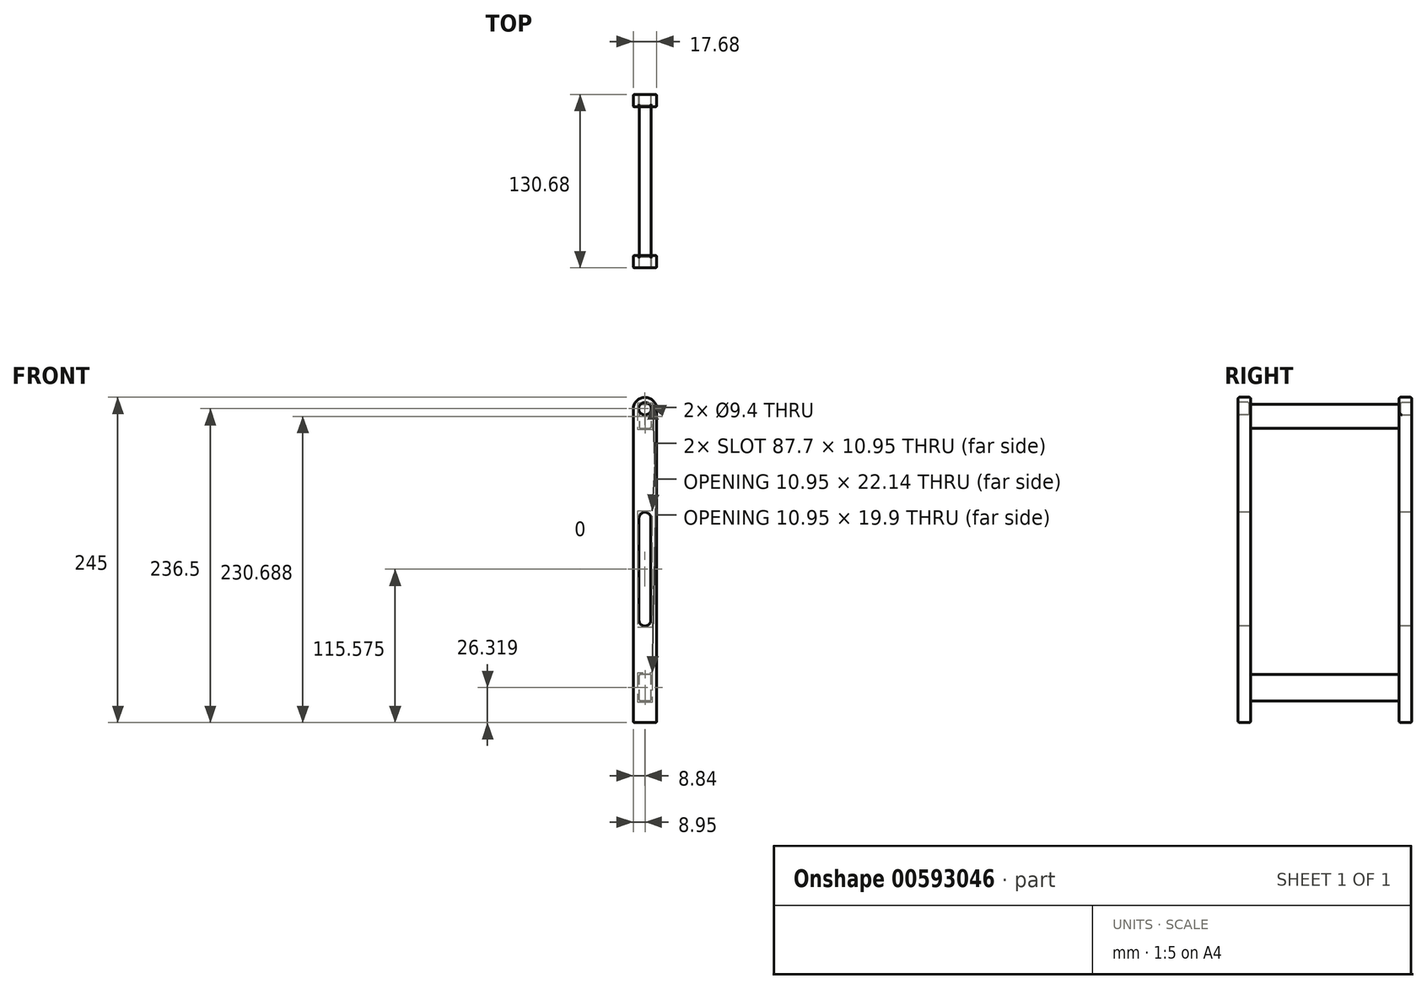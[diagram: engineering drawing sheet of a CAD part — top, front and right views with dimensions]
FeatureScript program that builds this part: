
annotation { "Feature Type Name" : "Feature", "Feature Type Description" : "" }
export const myFeature = defineFeature(function(context is Context, id is Id, definition is map)
    precondition{}
    {
        {
            var Q0;
            Q0=qCreatedBy(makeId("Front.planeOp"),FACE);
            var sketch = newSketch(context, id + "F0", { "sketchPlane" : qUnion([Q0])});
            skLineSegment(sketch, "E0.top", {"start": v(-8.84, -118.08) * mm, "end": v(8.84, -118.08) * mm});
            skLineSegment(sketch, "E0.left", {"start": v(-8.84, 118.08) * mm, "end": v(-8.84, -118.08) * mm});
            skLineSegment(sketch, "E0.right", {"start": v(8.84, 118.08) * mm, "end": v(8.84, -118.08) * mm});
            skPoint(sketch, "E0.middle", {"position": v(0, 0) * mm});
            skArc(sketch, "E1", {"start": v(-8.84, 118.08) * mm, "mid": v(0, 126.92) * mm, "end": v(8.84, 118.08) * mm});
            skSolve(sketch);
        }
        {
            var Q0;
            Q0=qSketchRegion(id+"F0",true);
            extrude(context, id + "F1", {"entities" : qUnion([Q0]), "depth" : 9.4 * mm});
        }
        {
            var Q0;
            Q0=makeQuery(id+"F1.opExtrude","CAP_FACE",FACE,{"disambiguationData":[OSD([sQuery(id+"F0.wireOp",EDGE,"E0.top"),sQuery(id+"F0.wireOp",EDGE,"E0.left"),sQuery(id+"F0.wireOp",EDGE,"E0.right"),sQuery(id+"F0.wireOp",EDGE,"E1")])],"isStart":false});
            var sketch = newSketch(context, id + "F2", { "sketchPlane" : qUnion([Q0])});
            skLineSegment(sketch, "E2.bottom", {"start": v(4.58, -101.83) * mm, "end": v(-4.37, -101.83) * mm});
            skLineSegment(sketch, "E2.top", {"start": v(4.58, -81.7) * mm, "end": v(-4.37, -81.7) * mm});
            skLineSegment(sketch, "E2.left", {"start": v(4.58, -101.83) * mm, "end": v(4.58, -81.7) * mm});
            skLineSegment(sketch, "E2.right", {"start": v(-4.37, -101.83) * mm, "end": v(-4.37, -81.7) * mm});
            skLineSegment(sketch, "E3.bottom", {"start": v(-4.36, 121.56) * mm, "end": v(4.59, 121.56) * mm});
            skLineSegment(sketch, "E3.top", {"start": v(-4.36, 103.66) * mm, "end": v(4.59, 103.66) * mm});
            skLineSegment(sketch, "E3.left", {"start": v(-4.36, 121.56) * mm, "end": v(-4.36, 103.66) * mm});
            skLineSegment(sketch, "E3.right", {"start": v(4.59, 121.56) * mm, "end": v(4.59, 103.66) * mm});
            skSolve(sketch);
        }
        {
            var Q0;
            Q0=makeQuery(id+"F2.imprint","IMPRINT",FACE,{"disambiguationData":[TD([[makeQuery(id+"F2.imprint","IMPRINT",EDGE,{"derivedFrom":sQuery(id+"F2.wireOp",EDGE,"E3.bottom")}),-1.0]])]});
            var Q1;
            Q1=makeQuery(id+"F2.imprint","IMPRINT",FACE,{"disambiguationData":[TD([[makeQuery(id+"F2.imprint","IMPRINT",EDGE,{"derivedFrom":sQuery(id+"F2.wireOp",EDGE,"E2.bottom")}),-1.0]])]});
            extrude(context, id + "F3", {"entities" : qUnion([Q0, Q1]), "operationType" : NewBodyOperationType.ADD, "depth" : 111.88 * mm});
        }
        {
            var Q0;
            Q0=makeQuery(id+"F3.opExtrude","CAP_FACE",FACE,{"disambiguationData":[OSD([sQuery(id+"F2.wireOp",EDGE,"E3.bottom"),sQuery(id+"F2.wireOp",EDGE,"E3.top"),sQuery(id+"F2.wireOp",EDGE,"E3.left"),sQuery(id+"F2.wireOp",EDGE,"E3.right")])],"isStart":false});
            var sketch = newSketch(context, id + "F4", { "sketchPlane" : qUnion([Q0])});
            skArc(sketch, "E4", {"start": v(8.84, 118.08) * mm, "mid": v(0, 126.92) * mm, "end": v(-8.84, 118.08) * mm});
            skLineSegment(sketch, "E5.bottom", {"start": v(-8.84, -118.08) * mm, "end": v(8.84, -118.08) * mm});
            skLineSegment(sketch, "E5.left", {"start": v(-8.84, -118.08) * mm, "end": v(-8.84, 118.08) * mm});
            skLineSegment(sketch, "E5.right", {"start": v(8.84, -118.08) * mm, "end": v(8.84, 118.08) * mm});
            skSolve(sketch);
        }
        {
            var Q0;
            Q0=qSketchRegion(id+"F4",true);
            extrude(context, id + "F5", {"entities" : qUnion([Q0]), "operationType" : NewBodyOperationType.ADD, "depth" : 9.4 * mm});
        }
        {
            var Q0;
            Q0=makeQuery(id+"F5.opExtrude","CAP_FACE",FACE,{"disambiguationData":[OSD([sQuery(id+"F4.wireOp",EDGE,"E4"),sQuery(id+"F4.wireOp",EDGE,"E5.bottom"),sQuery(id+"F4.wireOp",EDGE,"E5.left"),sQuery(id+"F4.wireOp",EDGE,"E5.right")])],"isStart":false});
            var sketch = newSketch(context, id + "F6", { "sketchPlane" : qUnion([Q0])});
            skArc(sketch, "E6", {"start": v(4.47, 35.87) * mm, "mid": v(0, 40.34) * mm, "end": v(-4.47, 35.87) * mm});
            skArc(sketch, "E7", {"start": v(-4.47, -40.88) * mm, "mid": v(0, -45.35) * mm, "end": v(4.47, -40.88) * mm});
            skLineSegment(sketch, "E8", {"start": v(-4.47, -40.88) * mm, "end": v(-4.47, 35.87) * mm});
            skLineSegment(sketch, "E9", {"start": v(4.47, 35.87) * mm, "end": v(4.48, -40.88) * mm});
            skCircle(sketch, "E10", {"center": v(0, 118.42) * mm, "radius": 4.7 * mm});
            skLineSegment(sketch, "E11", {"start": v(0, 40.34) * mm, "end": v(0, -45.35) * mm, "construction": true});
            skSolve(sketch);
        }
        {
            var Q0;
            Q0=makeQuery(id+"F6.imprint","IMPRINT",FACE,{"disambiguationData":[TD([[makeQuery(id+"F6.imprint","IMPRINT",EDGE,{"derivedFrom":sQuery(id+"F6.wireOp",EDGE,"E6")}),1.0]])]});
            extrude(context, id + "F7", {"entities" : qUnion([Q0]), "operationType" : NewBodyOperationType.REMOVE, "endBound" : BoundingType.THROUGH_ALL, "oppositeDirection" : true, "depth" : 25 * mm});
        }
        {
            var Q0;
            Q0=makeQuery(id+"F6.imprint","IMPRINT",FACE,{"disambiguationData":[TD([[makeQuery(id+"F6.imprint","IMPRINT",EDGE,{"derivedFrom":sQuery(id+"F6.wireOp",EDGE,"E10")}),1.0]])]});
            extrude(context, id + "F8", {"entities" : qUnion([Q0]), "operationType" : NewBodyOperationType.REMOVE, "oppositeDirection" : true, "depth" : 8.4 * mm});
        }
        {
            var Q0;
            Q0=makeQuery(id+"F1.opExtrude","CAP_FACE",FACE,{"disambiguationData":[OSD([sQuery(id+"F0.wireOp",EDGE,"E0.top"),sQuery(id+"F0.wireOp",EDGE,"E0.left"),sQuery(id+"F0.wireOp",EDGE,"E0.right"),sQuery(id+"F0.wireOp",EDGE,"E1")])],"isStart":true});
            var sketch = newSketch(context, id + "F9", { "sketchPlane" : qUnion([Q0])});
            skCircle(sketch, "E12", {"center": v(0, 118.42) * mm, "radius": 4.7 * mm});
            skSolve(sketch);
        }
        {
            var Q0;
            Q0=makeQuery(id+"F9.imprint","IMPRINT",FACE,{"disambiguationData":[TD([[makeQuery(id+"F9.imprint","IMPRINT",EDGE,{"derivedFrom":sQuery(id+"F9.wireOp",EDGE,"E12")}),1.0]])]});
            extrude(context, id + "F10", {"entities" : qUnion([Q0]), "operationType" : NewBodyOperationType.REMOVE, "oppositeDirection" : true, "depth" : 8.4 * mm});
        }
        {
            var Q0;
            Q0=makeQuery(id+"F5.opExtrude","CAP_FACE",FACE,{"disambiguationData":[OSD([sQuery(id+"F4.wireOp",EDGE,"E4"),sQuery(id+"F4.wireOp",EDGE,"E5.bottom"),sQuery(id+"F4.wireOp",EDGE,"E5.left"),sQuery(id+"F4.wireOp",EDGE,"E5.right")])],"isStart":false});
            var Q1;
            Q1=makeQuery(id+"F1.opExtrude","CAP_FACE",FACE,{"disambiguationData":[OSD([sQuery(id+"F0.wireOp",EDGE,"E0.top"),sQuery(id+"F0.wireOp",EDGE,"E0.left"),sQuery(id+"F0.wireOp",EDGE,"E0.right"),sQuery(id+"F0.wireOp",EDGE,"E1")])],"isStart":false});
            var Q2;
            Q2=makeQuery(id+"F3.opExtrude","SWEPT_FACE",FACE,{"disambiguationData":[OSD([sQuery(id+"F2.wireOp",EDGE,"E3.right")])]});
            var Q3;
            Q3=makeQuery(id+"F3.opExtrude","SWEPT_FACE",FACE,{"disambiguationData":[OSD([sQuery(id+"F2.wireOp",EDGE,"E3.bottom")])]});
            var Q4;
            Q4=makeQuery(id+"F5.opExtrude","CAP_FACE",FACE,{"disambiguationData":[OSD([sQuery(id+"F4.wireOp",EDGE,"E4"),sQuery(id+"F4.wireOp",EDGE,"E5.bottom"),sQuery(id+"F4.wireOp",EDGE,"E5.left"),sQuery(id+"F4.wireOp",EDGE,"E5.right")])],"isStart":true});
            var Q5;
            Q5=makeQuery(id+"F1.opExtrude","CAP_FACE",FACE,{"disambiguationData":[OSD([sQuery(id+"F0.wireOp",EDGE,"E0.top"),sQuery(id+"F0.wireOp",EDGE,"E0.left"),sQuery(id+"F0.wireOp",EDGE,"E0.right"),sQuery(id+"F0.wireOp",EDGE,"E1")])],"isStart":true});
            var Q6;
            Q6=makeQuery(id+"F3.opExtrude","SWEPT_FACE",FACE,{"disambiguationData":[OSD([sQuery(id+"F2.wireOp",EDGE,"E3.left")])]});
            var Q7;
            Q7=makeQuery(id+"F3.opExtrude","SWEPT_EDGE",EDGE,{"disambiguationData":[OSD([sQuery(id+"F2.wireOp",EDGE,"E3.top"),sQuery(id+"F2.wireOp",EDGE,"E3.right")])]});
            var Q8;
            Q8=makeQuery(id+"F3.opExtrude","SWEPT_FACE",FACE,{"disambiguationData":[OSD([sQuery(id+"F2.wireOp",EDGE,"E2.right")])]});
            var Q9;
            Q9=makeQuery(id+"F3.opExtrude","SWEPT_FACE",FACE,{"disambiguationData":[OSD([sQuery(id+"F2.wireOp",EDGE,"E2.left")])]});
            var Q10;
            Q10=makeQuery(id+"F3.opExtrude","SWEPT_FACE",FACE,{"disambiguationData":[OSD([sQuery(id+"F2.wireOp",EDGE,"E2.bottom")])]});
            var Q11;
            Q11=makeQuery(id+"F3.opExtrude","SWEPT_FACE",FACE,{"disambiguationData":[OSD([sQuery(id+"F2.wireOp",EDGE,"E2.top")])]});
            var Q12;
            Q12=makeQuery(id+"F1.opExtrude","SWEPT_FACE",FACE,{"disambiguationData":[OSD([sQuery(id+"F0.wireOp",EDGE,"E0.top")])]});
            var Q13;
            Q13=makeQuery(id+"F5.opExtrude","SWEPT_FACE",FACE,{"disambiguationData":[OSD([sQuery(id+"F4.wireOp",EDGE,"E5.bottom")])]});
            var Q14;
            Q14=makeQuery(id+"F10.boolean.opBoolean","COPY",EDGE,{"derivedFrom":makeQuery(id+"F10.opExtrude","CAP_EDGE",EDGE,{"disambiguationData":[OSD([sQuery(id+"F9.wireOp",EDGE,"E12")])],"isStart":false})});
            var Q15;
            Q15=makeQuery(id+"F8.boolean.opBoolean","COPY",EDGE,{"derivedFrom":makeQuery(id+"F8.opExtrude","CAP_EDGE",EDGE,{"disambiguationData":[OSD([sQuery(id+"F6.wireOp",EDGE,"E10")])],"isStart":false})});
            fillet(context, id + "F11", {"entities" : qUnion([Q0, Q1, Q2, Q3, Q4, Q5, Q6, Q7, Q8, Q9, Q10, Q11, Q12, Q13, Q14, Q15]), "radius" : 1 * mm, "tangentPropagation" : true, "allowEdgeOverflow" : false});
        }
    });
